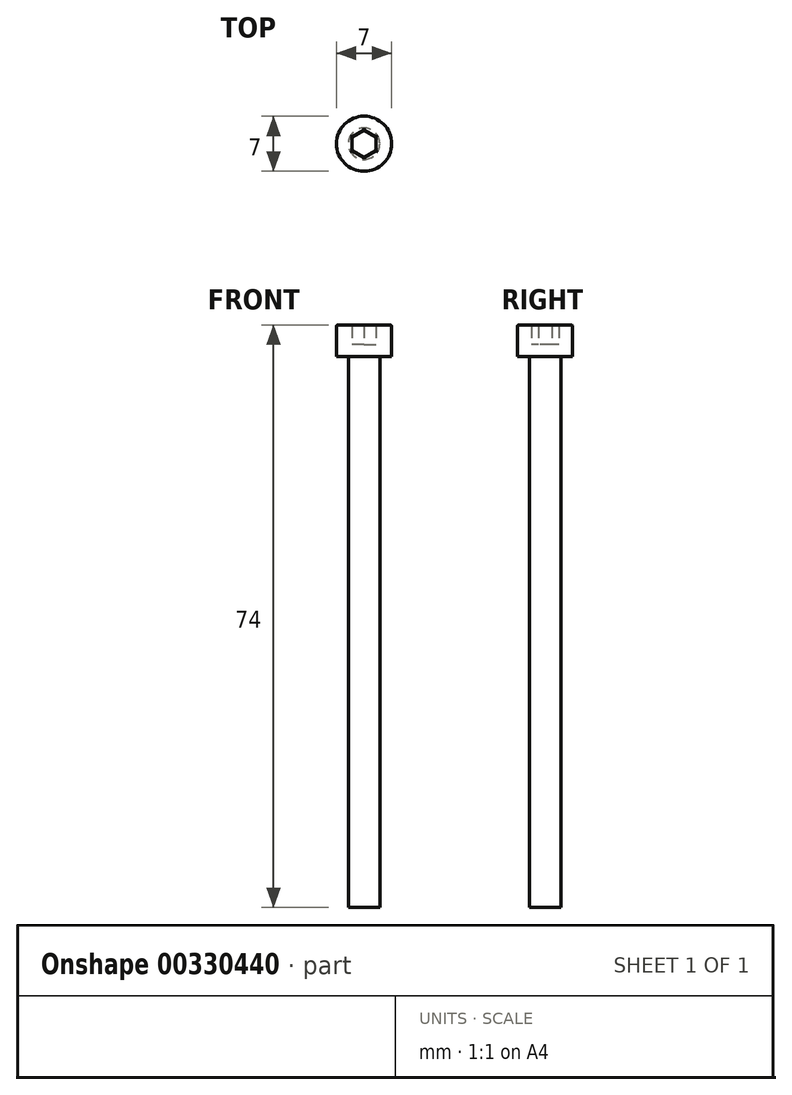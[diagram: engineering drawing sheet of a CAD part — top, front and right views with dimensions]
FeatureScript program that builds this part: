
annotation { "Feature Type Name" : "Feature", "Feature Type Description" : "" }
export const myFeature = defineFeature(function(context is Context, id is Id, definition is map)
    precondition{}
    {
        {
            var Q0;
            Q0=qCreatedBy(makeId("Top.planeOp"),FACE);
            var sketch = newSketch(context, id + "F0", { "sketchPlane" : qUnion([Q0])});
            skCircle(sketch, "E0", {"center": v(0, 0) * mm, "radius": 3.5 * mm});
            skCircle(sketch, "E1", {"center": v(0, 0) * mm, "radius": 2 * mm});
            skCircle(sketch, "E2.cCircle", {"center": v(0, 0) * mm, "radius": 1.5 * mm, "construction": true});
            skLineSegment(sketch, "E2.0", {"start": v(1.5, 0.87) * mm, "end": v(1.5, -0.87) * mm});
            skLineSegment(sketch, "E2.1", {"start": v(1.5, -0.87) * mm, "end": v(0, -1.73) * mm});
            skLineSegment(sketch, "E2.2", {"start": v(0, -1.73) * mm, "end": v(-1.5, -0.87) * mm});
            skLineSegment(sketch, "E2.3", {"start": v(-1.5, -0.87) * mm, "end": v(-1.5, 0.87) * mm});
            skLineSegment(sketch, "E2.4", {"start": v(-1.5, 0.87) * mm, "end": v(0, 1.73) * mm});
            skLineSegment(sketch, "E2.5", {"start": v(0, 1.73) * mm, "end": v(1.5, 0.87) * mm});
            skPoint(sketch, "E2.0.midPoint", {"position": v(1.5, 0) * mm});
            skSolve(sketch);
        }
        {
            var Q0;
            Q0=makeQuery(id+"F0.imprint","IMPRINT",FACE,{"disambiguationData":[TD([[makeQuery(id+"F0.imprint","IMPRINT",EDGE,{"derivedFrom":sQuery(id+"F0.wireOp",EDGE,"E0")}),1.0]])]});
            var Q1;
            Q1=makeQuery(id+"F0.imprint","IMPRINT",FACE,{"disambiguationData":[TD([[makeQuery(id+"F0.imprint","IMPRINT",EDGE,{"derivedFrom":sQuery(id+"F0.wireOp",EDGE,"E1")}),1.0]])]});
            extrude(context, id + "F1", {"entities" : qUnion([Q0, Q1]), "depth" : 4 * mm});
        }
        {
            var Q0;
            Q0=makeQuery(id+"F0.imprint","IMPRINT",FACE,{"disambiguationData":[TD([[makeQuery(id+"F0.imprint","IMPRINT",EDGE,{"derivedFrom":sQuery(id+"F0.wireOp",EDGE,"E1")}),1.0]])]});
            var Q1;
            Q1=makeQuery(id+"F0.imprint","IMPRINT",FACE,{"disambiguationData":[TD([[makeQuery(id+"F0.imprint","IMPRINT",EDGE,{"derivedFrom":sQuery(id+"F0.wireOp",EDGE,"E2.0")}),-1.0]])]});
            extrude(context, id + "F2", {"entities" : qUnion([Q0, Q1]), "operationType" : NewBodyOperationType.ADD, "oppositeDirection" : true, "depth" : 70 * mm});
        }
        {
            var Q0;
            Q0=makeQuery(id+"F0.imprint","IMPRINT",FACE,{"disambiguationData":[TD([[makeQuery(id+"F0.imprint","IMPRINT",EDGE,{"derivedFrom":sQuery(id+"F0.wireOp",EDGE,"E2.0")}),-1.0]])]});
            extrude(context, id + "F3", {"entities" : qUnion([Q0]), "operationType" : NewBodyOperationType.ADD, "depth" : 1.5 * mm});
        }
        {
            var Q0;
            Q0=makeQuery(id+"F1.opExtrude","CAP_EDGE",EDGE,{"disambiguationData":[OSD([sQuery(id+"F0.wireOp",EDGE,"E0")])],"isStart":false});
            var Q1;
            Q1=makeQuery(id+"F1.opExtrude","CAP_EDGE",EDGE,{"disambiguationData":[OSD([sQuery(id+"F0.wireOp",EDGE,"E2.2")])],"isStart":false});
            var Q2;
            Q2=makeQuery(id+"F1.opExtrude","CAP_EDGE",EDGE,{"disambiguationData":[OSD([sQuery(id+"F0.wireOp",EDGE,"E2.3")])],"isStart":false});
            var Q3;
            Q3=makeQuery(id+"F1.opExtrude","CAP_EDGE",EDGE,{"disambiguationData":[OSD([sQuery(id+"F0.wireOp",EDGE,"E2.4")])],"isStart":false});
            var Q4;
            Q4=makeQuery(id+"F1.opExtrude","CAP_EDGE",EDGE,{"disambiguationData":[OSD([sQuery(id+"F0.wireOp",EDGE,"E2.5")])],"isStart":false});
            var Q5;
            Q5=makeQuery(id+"F1.opExtrude","CAP_EDGE",EDGE,{"disambiguationData":[OSD([sQuery(id+"F0.wireOp",EDGE,"E2.0")])],"isStart":false});
            var Q6;
            Q6=makeQuery(id+"F1.opExtrude","CAP_EDGE",EDGE,{"disambiguationData":[OSD([sQuery(id+"F0.wireOp",EDGE,"E2.1")])],"isStart":false});
            fillet(context, id + "F4", {"entities" : qUnion([Q0, Q1, Q2, Q3, Q4, Q5, Q6]), "radius" : 0.2 * mm, "tangentPropagation" : true, "allowEdgeOverflow" : false});
        }
    });
